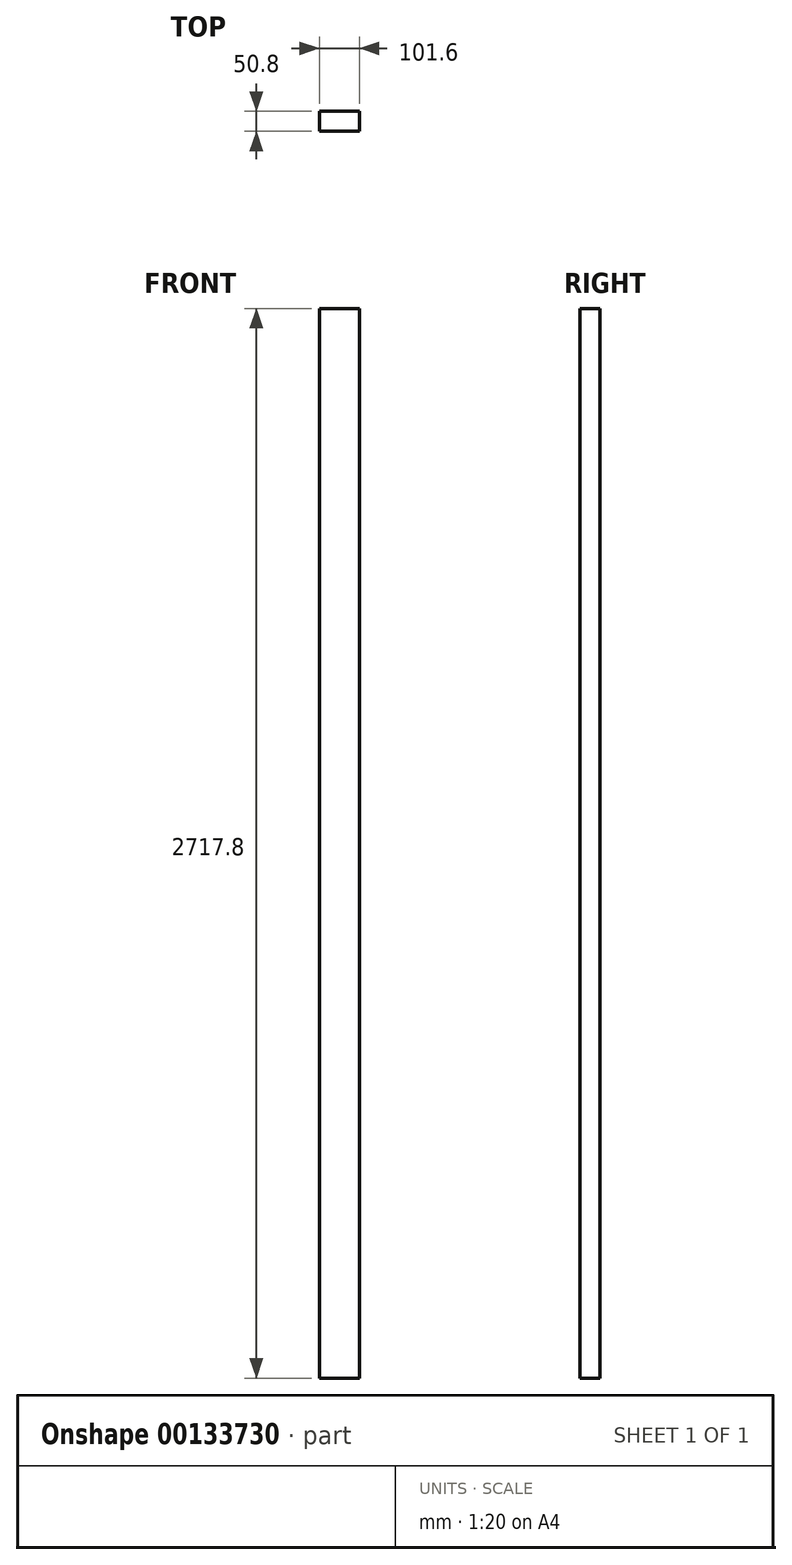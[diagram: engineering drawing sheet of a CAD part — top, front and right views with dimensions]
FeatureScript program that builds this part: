
annotation { "Feature Type Name" : "Feature", "Feature Type Description" : "" }
export const myFeature = defineFeature(function(context is Context, id is Id, definition is map)
    precondition{}
    {
        {
            var Q0;
            Q0=qCreatedBy(makeId("Top.planeOp"),FACE);
            var sketch = newSketch(context, id + "F0", { "sketchPlane" : qUnion([Q0])});
            skLineSegment(sketch, "E0.bottom", {"start": v(0, 0) * mm, "end": v(101.6, 0) * mm});
            skLineSegment(sketch, "E0.top", {"start": v(0, -50.8) * mm, "end": v(101.6, -50.8) * mm});
            skLineSegment(sketch, "E0.left", {"start": v(0, 0) * mm, "end": v(0, -50.8) * mm});
            skLineSegment(sketch, "E0.right", {"start": v(101.6, 0) * mm, "end": v(101.6, -50.8) * mm});
            skSolve(sketch);
        }
        {
            var Q0;
            Q0 = qSketchRegion(id + "F0", true);
            extrude(context, id + "F1", {"entities" : qUnion([Q0]), "depth" : 2717.8 * mm});
        }
    });
